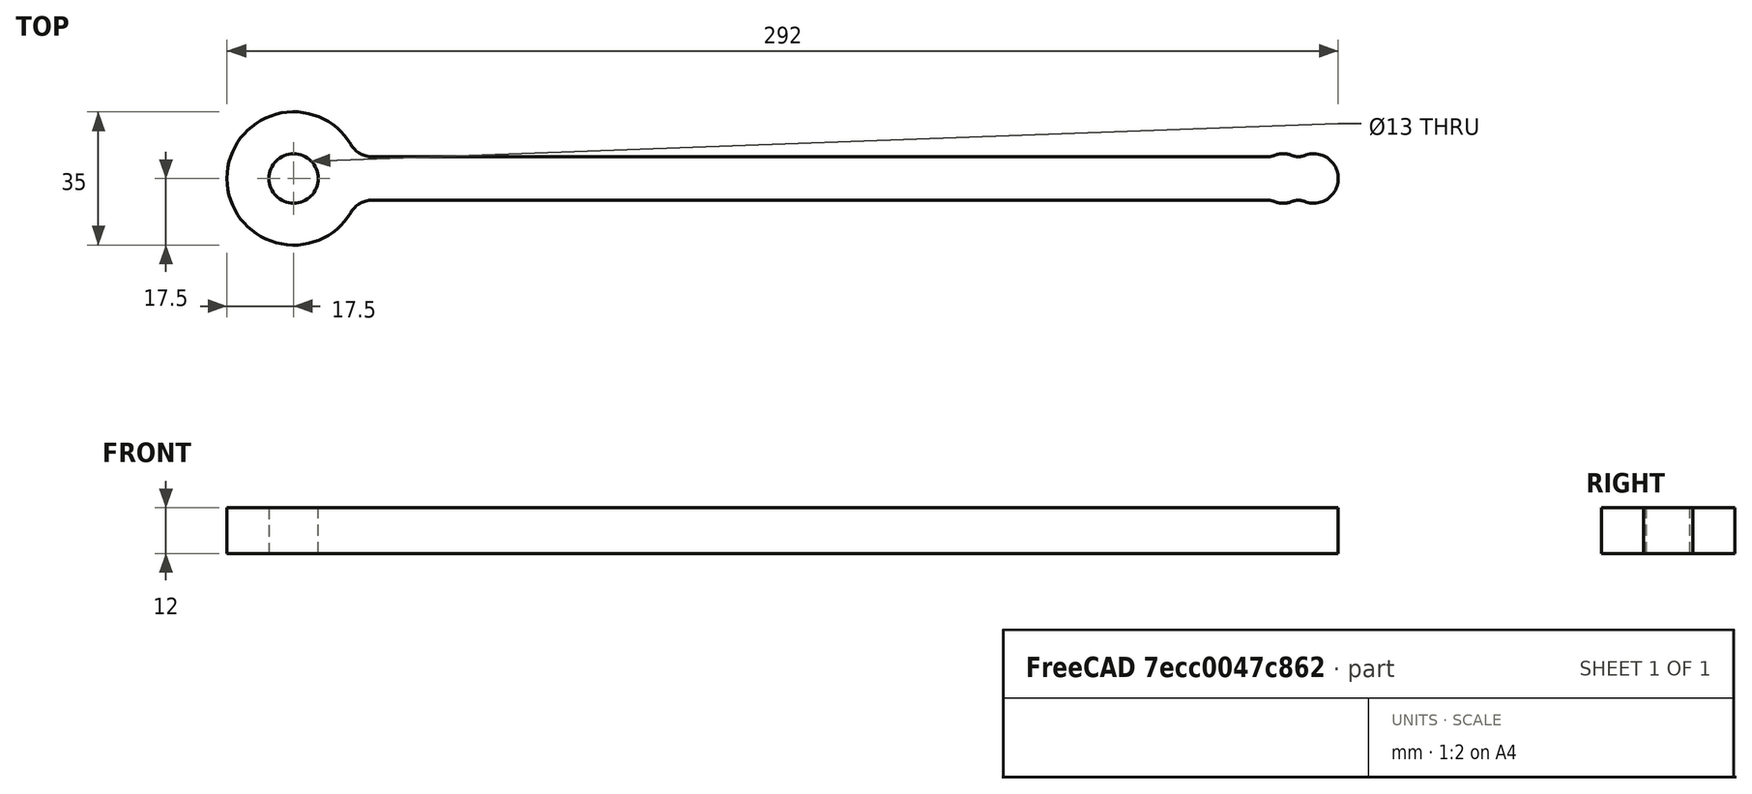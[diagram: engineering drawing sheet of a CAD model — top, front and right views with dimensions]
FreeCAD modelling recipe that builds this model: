
FCSTD DOCUMENT  (FreeCAD 0.19R24366 (Git))
Label: Installation preload tool
License: All rights reserved
LicenseURL: http://en.wikipedia.org/wiki/All_rights_reserved
objects: Sketcher::SketchObject×1, PartDesign::Pad×1, PartDesign::Body×1
note: 4 computed .brp shape members not serialized (recipe doc carries the construction recipe); baked Part::Feature solids carry a one-line shape summary decoded from their .brp

FEATURE [Sketcher::SketchObject] Sketch
  FullyConstrained = true
  MapMode = 5
  Support = -> [XY_Plane]
  sketch-geometry (18):
    g0: ArcOfCircle CenterX=-4 CenterY=0 CenterZ=0 NormalX=0 NormalY=0 NormalZ=1 AngleXU=0 Radius=6.5 StartAngle=1.17997 EndAngle=1.96162
    g1: ArcOfCircle CenterX=4 CenterY=0 CenterZ=0 NormalX=0 NormalY=0 NormalZ=1 AngleXU=0 Radius=6.5 StartAngle=4.32156 EndAngle=8.24481
    g2: GeomPoint X=0 Y=-5.12348 Z=0
    g3: GeomPoint X=0 Y=5.12348 Z=0
    g4: LineSegment StartX=-7.99999 StartY=5.70825 StartZ=0 EndX=-243.337 EndY=5.70825 EndZ=0
    g5: LineSegment StartX=-7.99999 StartY=-5.70825 StartZ=0 EndX=-243.337 EndY=-5.70825 EndZ=0
    g6: ArcOfCircle CenterX=-4 CenterY=0 CenterZ=0 NormalX=0 NormalY=0 NormalZ=1 AngleXU=0 Radius=6.5 StartAngle=4.32156 EndAngle=5.10322
    g7: ArcOfCircle CenterX=-1.6e-15 CenterY=9.70824 CenterZ=0 NormalX=0 NormalY=0 NormalZ=1 AngleXU=0 Radius=4 StartAngle=4.32156 EndAngle=5.10322
    g8: ArcOfCircle CenterX=-2e-16 CenterY=-9.70824 CenterZ=0 NormalX=0 NormalY=0 NormalZ=1 AngleXU=0 Radius=4 StartAngle=1.17997 EndAngle=1.96162
    g9: ArcOfCircle CenterX=-7.99999 CenterY=9.70825 CenterZ=0 NormalX=0 NormalY=0 NormalZ=1 AngleXU=0 Radius=4 StartAngle=4.71239 EndAngle=5.10321
    g10: ArcOfCircle CenterX=-7.99999 CenterY=-9.70825 CenterZ=0 NormalX=0 NormalY=0 NormalZ=1 AngleXU=0 Radius=4 StartAngle=1.17997 EndAngle=1.5708
    g11: GeomPoint X=0 Y=5.70824 Z=0
    g12: LineSegment StartX=-7.99999 StartY=5.70825 StartZ=0 EndX=0 EndY=5.70824 EndZ=0
    g13: Circle CenterX=-264 CenterY=0 CenterZ=0 NormalX=0 NormalY=0 NormalZ=1 AngleXU=0 Radius=6.5
    g14: ArcOfCircle CenterX=-264 CenterY=0 CenterZ=0 NormalX=0 NormalY=0 NormalZ=1 AngleXU=0 Radius=17.5 StartAngle=0.533647 EndAngle=5.74954
    g15: ArcOfCircle CenterX=-243.337 CenterY=12.2082 CenterZ=0 NormalX=0 NormalY=0 NormalZ=1 AngleXU=0 Radius=6.5 StartAngle=3.67524 EndAngle=4.71239
    g16: ArcOfCircle CenterX=-243.337 CenterY=-12.2082 CenterZ=0 NormalX=0 NormalY=0 NormalZ=1 AngleXU=0 Radius=6.5 StartAngle=1.5708 EndAngle=2.60795
    g17: LineSegment StartX=-243.337 StartY=5.70825 StartZ=0 EndX=-243.337 EndY=-5.70825 EndZ=0
  constraints (44):
    c: PointOnObject(g0,g-1)
    c: Symmetric(g0,g1,g-2)
    c: DistanceX(g0,g1) = 8
    c: Equal(g0,g1)
    c: PointOnObject(g2,g-2)
    c: PointOnObject(g3,g-2)
    c: PointOnObject(g3,g0)
    c: PointOnObject(g2,g0)
    c: Horizontal(g4)
    c: Horizontal(g5)
    c: Equal(g0,g6)
    c: Coincident(g0,g6)
    c: Tangent(g0,g7) = 1.5708
    c: Tangent(g1,g7) = 1.5708
    c: Tangent(g6,g8) = 1.5708
    c: Tangent(g1,g8) = 1.5708
    c: Equal(g7,g8)
    c: Radius(g7) = 4
    c: Tangent(g0,g9) = 1.5708
    c: Tangent(g4,g9) = 1.5708
    c: Tangent(g6,g10) = 1.5708
    c: Tangent(g5,g10) = -1.5708
    c: Equal(g9,g10)
    c: Equal(g10,g7)
    c: PointOnObject(g11,g-2)
    c: PointOnObject(g11,g7)
    c: Coincident(g12,g4)
    c: Coincident(g12,g11)
    c: Tangent(g12,g9)
    c: Diameter(g13) = 13
    c: Coincident(g14,g13)
    c: Diameter(g14) = 35
    c: Tangent(g4,g15) = 1.5708
    c: Tangent(g14,g15) = 1.5708
    c: Tangent(g14,g16) = 1.5708
    c: Tangent(g5,g16) = -1.5708
    c: Equal(g15,g16)
    c: Equal(g15,g13)
    c: PointOnObject(g13,g-1)
    c: DistanceX(g13,g0) = 260
    c: Coincident(g17,g4)
    c: Coincident(g17,g5)
    c: Vertical(g17)
    c: Diameter(g1) = 13
FEATURE [PartDesign::Pad] Pad
  Direction = (1,1,1)
  Length = 12
  Length2 = 100
  Profile = -> Sketch
  Type = 0
FEATURE [PartDesign::Body] Body
  Group = -> [Sketch,Pad]
  Origin = -> Origin
  Tip = -> Pad
